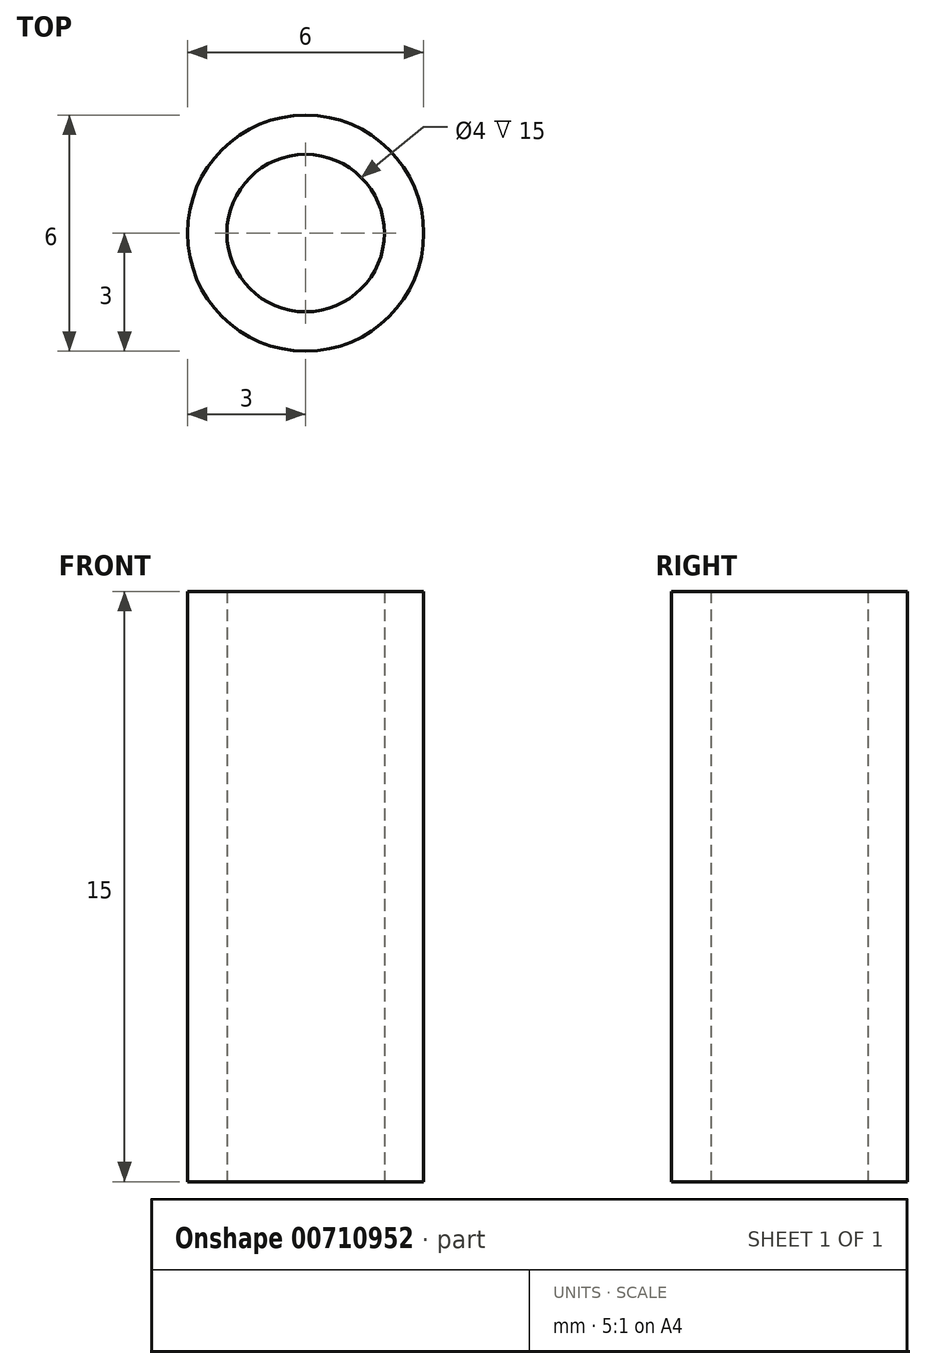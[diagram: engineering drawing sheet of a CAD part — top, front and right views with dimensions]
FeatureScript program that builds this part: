
annotation { "Feature Type Name" : "Feature", "Feature Type Description" : "" }
export const myFeature = defineFeature(function(context is Context, id is Id, definition is map)
    precondition{}
    {
        {
            var Q0;
            Q0=qCreatedBy(makeId("Top.planeOp"),FACE);
            var sketch = newSketch(context, id + "F0", { "sketchPlane" : qUnion([Q0])});
            skCircle(sketch, "E0", {"center": v(0, 0) * mm, "radius": 2 * mm});
            skCircle(sketch, "E1", {"center": v(0, 0) * mm, "radius": 3 * mm});
            skSolve(sketch);
        }
        {
            var Q0;
            Q0=makeQuery(id+"F0.imprint","IMPRINT",FACE,{"disambiguationData":[TD([[makeQuery(id+"F0.imprint","IMPRINT",EDGE,{"derivedFrom":sQuery(id+"F0.wireOp",EDGE,"E0")}),-1.0]])]});
            extrude(context, id + "F1", {"entities" : qUnion([Q0]), "depth" : 15 * mm, "offsetDistance" : 25 * mm});
        }
    });
